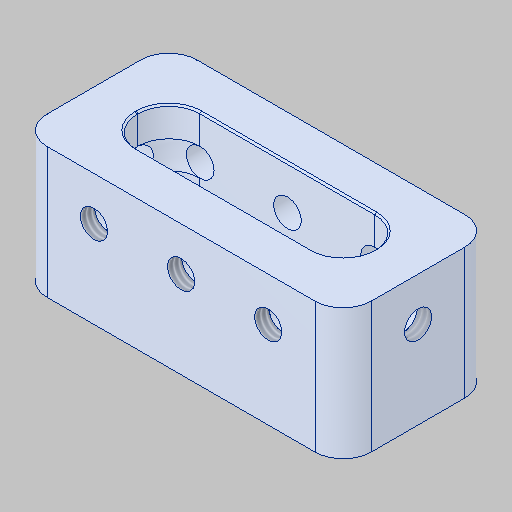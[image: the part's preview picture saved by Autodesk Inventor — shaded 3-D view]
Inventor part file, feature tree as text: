
AUTODESK INVENTOR PART (.ipt)
format: ipt  version: 2023.5 (Build 275446000, 446)  size: 365,056 bytes
history: native  units: in
note: dims shown in document units (in); Inventor stores cm internally (conversion verified against a paired STEP export)
features: sketch x4, other x3
ambient origin geometry x8: Origin, YZ Plane, XZ Plane, XY Plane, X Axis, Y Axis, Z Axis, Center Point
bodies: Solid1 (feature_tree)
feature tree (7):
  other  "GP4-003.ipt"
  other  "Solid1::GP4-003.ipt"
  other  "TaggingFeature1"
  sketch  "Sketch1"  dims[d0=0.3937in]
  sketch  "Sketch2"
  sketch  "Sketch3"
  sketch  "Sketch4"
